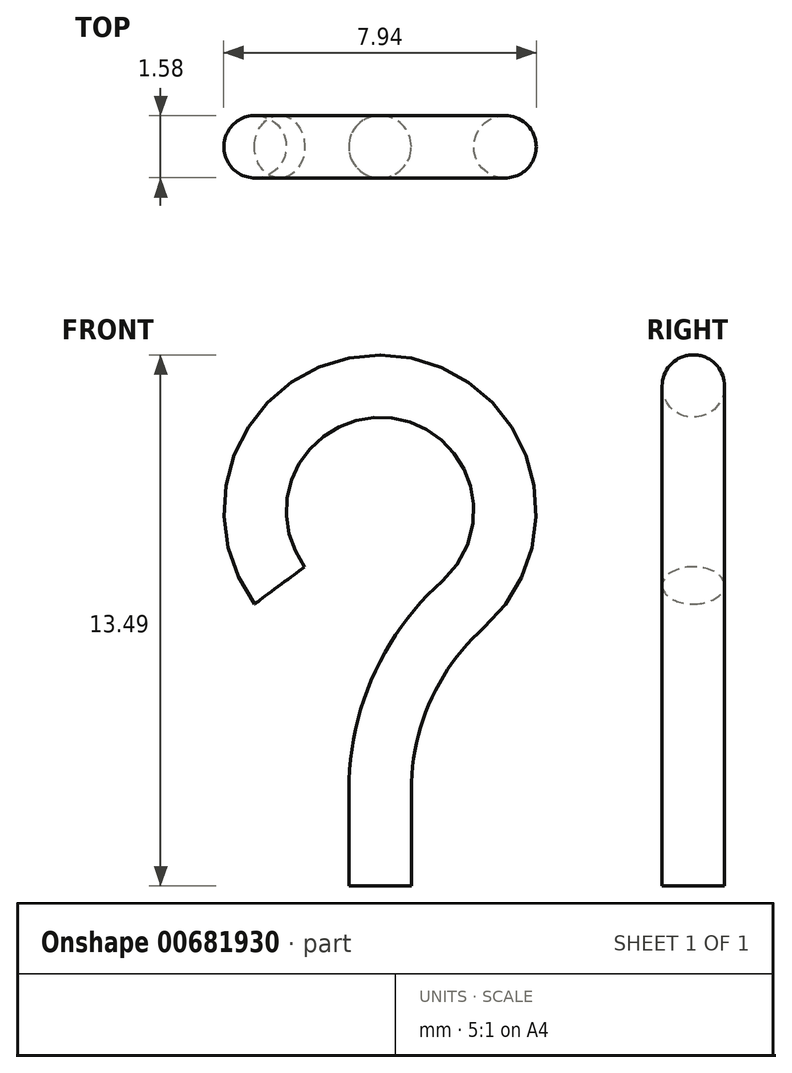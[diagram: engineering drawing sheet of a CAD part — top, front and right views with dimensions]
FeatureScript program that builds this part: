
annotation { "Feature Type Name" : "Feature", "Feature Type Description" : "" }
export const myFeature = defineFeature(function(context is Context, id is Id, definition is map)
    precondition{}
    {
        {
            var Q0;
            Q0=qCreatedBy(makeId("Front.planeOp"),FACE);
            var sketch = newSketch(context, id + "F0", { "sketchPlane" : qUnion([Q0])});
            skLineSegment(sketch, "E0", {"start": v(0, 0) * mm, "end": v(0, 2.43) * mm});
            skArc(sketch, "E1", {"start": v(2.12, 7.16) * mm, "mid": v(0.32, 12.68) * mm, "end": v(-2.55, 7.63) * mm});
            skLineSegment(sketch, "E2", {"start": v(0, 9.53) * mm, "end": v(-2.55, 7.63) * mm});
            skArc(sketch, "E3.filletArc", {"start": v(2.12, 7.16) * mm, "mid": v(0.55, 5.02) * mm, "end": v(0, 2.43) * mm});
            skSolve(sketch);
        }
        {
            var Q0;
            Q0=qCreatedBy(makeId("Top.planeOp"),FACE);
            var sketch = newSketch(context, id + "F1", { "sketchPlane" : qUnion([Q0])});
            skCircle(sketch, "E4", {"center": v(0, 0) * mm, "radius": 0.8 * mm});
            skSolve(sketch);
        }
        {
            var Q0;
            Q0=makeQuery(id+"F1.imprint","IMPRINT",FACE,{"disambiguationData":[TD([[makeQuery(id+"F1.imprint","IMPRINT",EDGE,{"derivedFrom":sQuery(id+"F1.wireOp",EDGE,"E4")}),1.0]])]});
            var Q1;
            Q1=sQuery(id+"F0.wireOp",EDGE,"E0");
            var Q2;
            Q2=sQuery(id+"F0.wireOp",EDGE,"E3.filletArc");
            var Q3;
            Q3=sQuery(id+"F0.wireOp",EDGE,"E1");
            sweep(context, id + "F2", {"profiles" : qUnion([Q0]), "path" : qUnion([Q1, Q2, Q3])});
        }
    });
